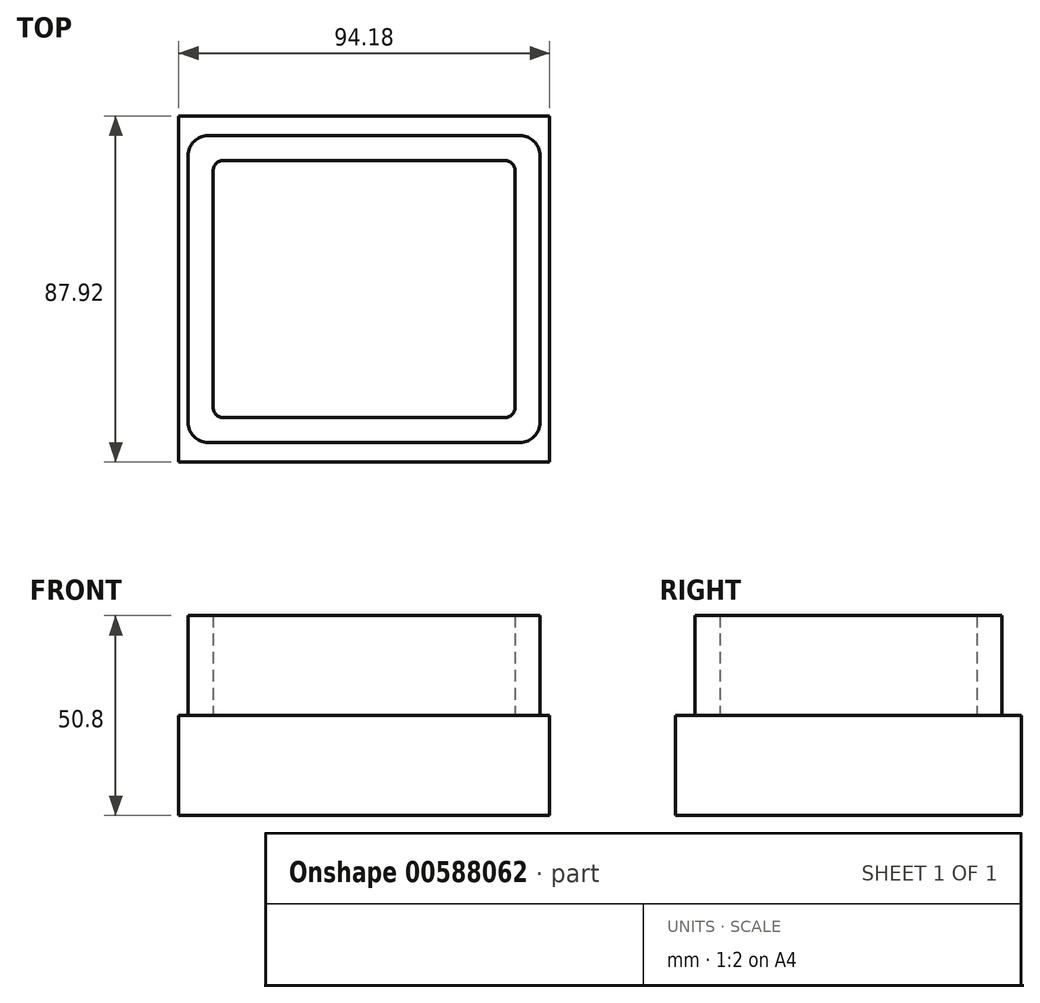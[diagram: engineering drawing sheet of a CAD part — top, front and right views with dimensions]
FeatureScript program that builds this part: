
annotation { "Feature Type Name" : "Feature", "Feature Type Description" : "" }
export const myFeature = defineFeature(function(context is Context, id is Id, definition is map)
    precondition{}
    {
        {
            var Q0;
            Q0=qCreatedBy(makeId("Top.planeOp"),FACE);
            var sketch = newSketch(context, id + "F0", { "sketchPlane" : qUnion([Q0])});
            skLineSegment(sketch, "E0.bottom", {"start": v(-44.7, 39) * mm, "end": v(44.7, 39) * mm});
            skLineSegment(sketch, "E0.top", {"start": v(-44.7, -39) * mm, "end": v(44.7, -39) * mm});
            skLineSegment(sketch, "E0.left", {"start": v(-44.7, 39) * mm, "end": v(-44.7, -39) * mm});
            skLineSegment(sketch, "E0.right", {"start": v(44.7, 39) * mm, "end": v(44.7, -39) * mm});
            skPoint(sketch, "E0.middle", {"position": v(0, 0) * mm});
            skLineSegment(sketch, "E1.0", {"start": v(38.34, 32.64) * mm, "end": v(38.34, -32.64) * mm});
            skLineSegment(sketch, "E1.1", {"start": v(-38.34, 32.64) * mm, "end": v(38.34, 32.64) * mm});
            skLineSegment(sketch, "E1.2", {"start": v(-38.34, 32.64) * mm, "end": v(-38.34, -32.64) * mm});
            skLineSegment(sketch, "E1.3", {"start": v(-38.34, -32.64) * mm, "end": v(38.34, -32.64) * mm});
            skSolve(sketch);
        }
        {
            var Q0;
            Q0 = qSketchRegion(id + "F0", true);
            extrude(context, id + "F1", {"entities" : qUnion([Q0]), "depth" : 25.4 * mm, "offsetDistance" : 25.4 * mm});
        }
        {
            var Q0;
            Q0=makeQuery(id+"F1.opExtrude","SWEPT_EDGE",EDGE,{"disambiguationData":[OSD([sQuery(id+"F0.wireOp",EDGE,"E0.top"),sQuery(id+"F0.wireOp",EDGE,"E0.left")])]});
            var Q1;
            Q1=makeQuery(id+"F1.opExtrude","SWEPT_EDGE",EDGE,{"disambiguationData":[OSD([sQuery(id+"F0.wireOp",EDGE,"E0.top"),sQuery(id+"F0.wireOp",EDGE,"E0.right")])]});
            var Q2;
            Q2=makeQuery(id+"F1.opExtrude","SWEPT_EDGE",EDGE,{"disambiguationData":[OSD([sQuery(id+"F0.wireOp",EDGE,"E0.bottom"),sQuery(id+"F0.wireOp",EDGE,"E0.right")])]});
            var Q3;
            Q3=makeQuery(id+"F1.opExtrude","SWEPT_EDGE",EDGE,{"disambiguationData":[OSD([sQuery(id+"F0.wireOp",EDGE,"E0.bottom"),sQuery(id+"F0.wireOp",EDGE,"E0.left")])]});
            fillet(context, id + "F2", {"entities" : qUnion([Q0, Q1, Q2, Q3]), "radius" : 5.08 * mm, "tangentPropagation" : true, "allowEdgeOverflow" : false});
        }
        {
            var Q0;
            Q0=makeQuery(id+"F1.opExtrude","SWEPT_EDGE",EDGE,{"disambiguationData":[OSD([sQuery(id+"F0.wireOp",EDGE,"E1.1"),sQuery(id+"F0.wireOp",EDGE,"E1.2")])]});
            var Q1;
            Q1=makeQuery(id+"F1.opExtrude","SWEPT_EDGE",EDGE,{"disambiguationData":[OSD([sQuery(id+"F0.wireOp",EDGE,"E1.0"),sQuery(id+"F0.wireOp",EDGE,"E1.1")])]});
            var Q2;
            Q2=makeQuery(id+"F1.opExtrude","SWEPT_EDGE",EDGE,{"disambiguationData":[OSD([sQuery(id+"F0.wireOp",EDGE,"E1.0"),sQuery(id+"F0.wireOp",EDGE,"E1.3")])]});
            var Q3;
            Q3=makeQuery(id+"F1.opExtrude","SWEPT_EDGE",EDGE,{"disambiguationData":[OSD([sQuery(id+"F0.wireOp",EDGE,"E1.2"),sQuery(id+"F0.wireOp",EDGE,"E1.3")])]});
            fillet(context, id + "F3", {"entities" : qUnion([Q0, Q1, Q2, Q3]), "radius" : 2.54 * mm, "tangentPropagation" : true, "allowEdgeOverflow" : false});
        }
        {
            var Q0;
            Q0=qCreatedBy(makeId("Top.planeOp"),FACE);
            var sketch = newSketch(context, id + "F4", { "sketchPlane" : qUnion([Q0])});
            skLineSegment(sketch, "E2.bottom", {"start": v(47.09, 43.96) * mm, "end": v(-47.09, 43.96) * mm});
            skLineSegment(sketch, "E2.top", {"start": v(47.09, -43.96) * mm, "end": v(-47.09, -43.96) * mm});
            skLineSegment(sketch, "E2.left", {"start": v(47.09, 43.96) * mm, "end": v(47.09, -43.96) * mm});
            skLineSegment(sketch, "E2.right", {"start": v(-47.09, 43.96) * mm, "end": v(-47.09, -43.96) * mm});
            skPoint(sketch, "E2.middle", {"position": v(0, 0) * mm});
            skSolve(sketch);
        }
        {
            var Q0;
            Q0=makeQuery(id+"F4.imprint","IMPRINT",FACE,{"disambiguationData":[TD([[makeQuery(id+"F4.imprint","IMPRINT",EDGE,{"derivedFrom":sQuery(id+"F4.wireOp",EDGE,"E2.bottom")}),1.0]])]});
            extrude(context, id + "F5", {"entities" : qUnion([Q0]), "operationType" : NewBodyOperationType.ADD, "oppositeDirection" : true, "depth" : 25.4 * mm, "offsetDistance" : 25.4 * mm});
        }
    });
